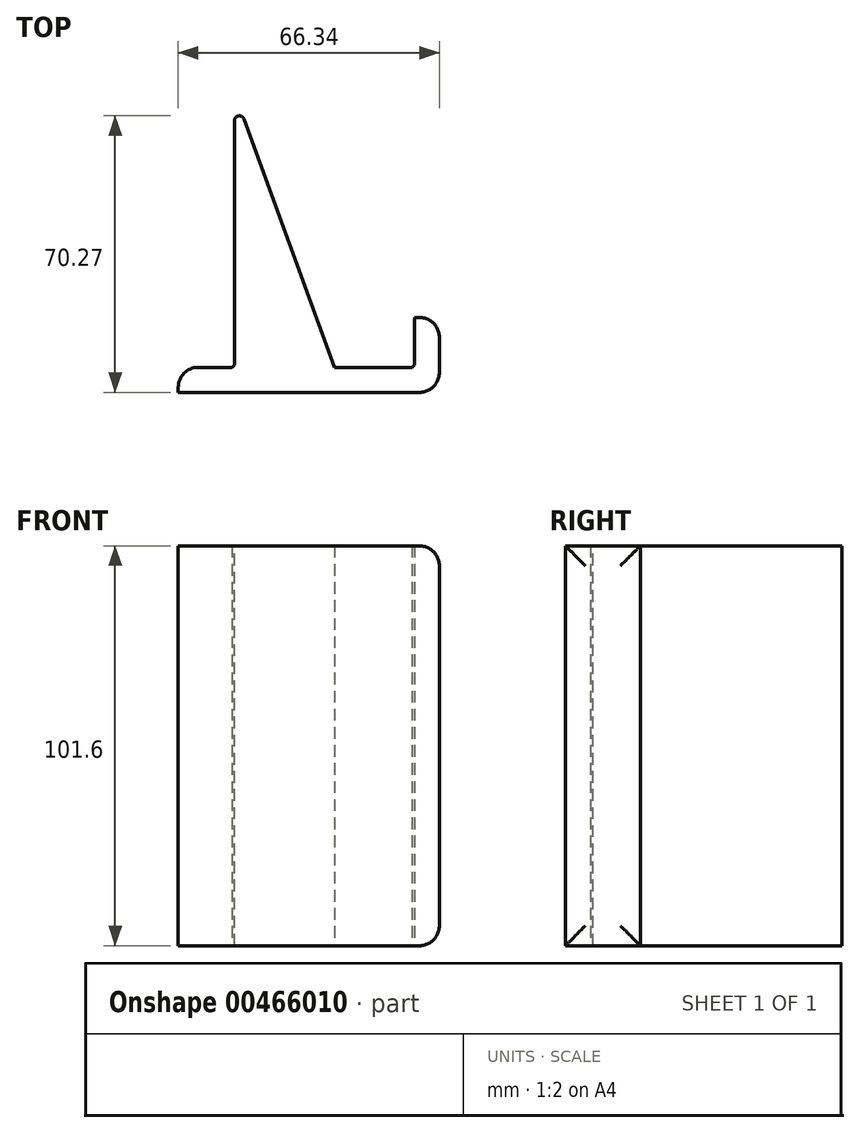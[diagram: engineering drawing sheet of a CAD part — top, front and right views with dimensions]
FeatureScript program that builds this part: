
annotation { "Feature Type Name" : "Feature", "Feature Type Description" : "" }
export const myFeature = defineFeature(function(context is Context, id is Id, definition is map)
    precondition{}
    {
        {
            var Q0;
            Q0=qCreatedBy(makeId("Top.planeOp"),FACE);
            var sketch = newSketch(context, id + "F0", { "sketchPlane" : qUnion([Q0])});
            skLineSegment(sketch, "E0", {"start": v(0, 76.2) * mm, "end": v(0, 6.35) * mm});
            skLineSegment(sketch, "E1", {"start": v(0, 6.35) * mm, "end": v(-14.25, 6.35) * mm});
            skLineSegment(sketch, "E2", {"start": v(-14.25, 6.35) * mm, "end": v(-14.25, 0) * mm});
            skLineSegment(sketch, "E3", {"start": v(-14.25, 0) * mm, "end": v(0, 0) * mm});
            skLineSegment(sketch, "E4", {"start": v(0, 0) * mm, "end": v(52.1, 0) * mm});
            skLineSegment(sketch, "E5", {"start": v(52.1, 0) * mm, "end": v(52.1, 19.05) * mm});
            skLineSegment(sketch, "E6", {"start": v(52.1, 19.05) * mm, "end": v(45.74, 19.05) * mm});
            skLineSegment(sketch, "E7", {"start": v(45.74, 19.05) * mm, "end": v(45.74, 6.35) * mm});
            skLineSegment(sketch, "E8", {"start": v(45.74, 6.35) * mm, "end": v(25.42, 6.35) * mm});
            skLineSegment(sketch, "E9", {"start": v(25.42, 6.35) * mm, "end": v(0, 76.2) * mm});
            skSolve(sketch);
        }
        {
            var Q0;
            Q0=makeQuery(id+"F0.imprint","IMPRINT",FACE,{"disambiguationData":[TD([[makeQuery(id+"F0.imprint","IMPRINT",EDGE,{"derivedFrom":sQuery(id+"F0.wireOp",EDGE,"E0")}),1.0]])]});
            extrude(context, id + "F1", {"entities" : qUnion([Q0]), "endBound" : BoundingType.SYMMETRIC, "depth" : 101.6 * mm});
        }
        {
            var Q0;
            Q0=makeQuery(id+"F1.opExtrude","SWEPT_EDGE",EDGE,{"disambiguationData":[OSD([sQuery(id+"F0.wireOp",EDGE,"E0"),sQuery(id+"F0.wireOp",EDGE,"E9")])]});
            fillet(context, id + "F2", {"entities" : qUnion([Q0]), "radius" : 1.27 * mm, "tangentPropagation" : true, "allowEdgeOverflow" : false});
        }
        {
            var Q0;
            Q0=makeQuery(id+"F1.opExtrude","SWEPT_FACE",FACE,{"disambiguationData":[OSD([sQuery(id+"F0.wireOp",EDGE,"E5")])]});
            fillet(context, id + "F3", {"entities" : qUnion([Q0]), "radius" : 5.08 * mm, "tangentPropagation" : true, "allowEdgeOverflow" : false});
        }
        {
            var Q0;
            Q0=makeQuery(id+"F1.opExtrude","SWEPT_EDGE",EDGE,{"disambiguationData":[OSD([sQuery(id+"F0.wireOp",EDGE,"E7"),sQuery(id+"F0.wireOp",EDGE,"E8")])]});
            var Q1;
            Q1=makeQuery(id+"F1.opExtrude","SWEPT_EDGE",EDGE,{"disambiguationData":[OSD([sQuery(id+"F0.wireOp",EDGE,"E0"),sQuery(id+"F0.wireOp",EDGE,"E1")])]});
            chamfer(context, id + "F4", {"entities" : qUnion([Q0, Q1]), "width" : 0.64 * mm, "tangentPropagation" : true});
        }
        {
            var Q0;
            Q0=makeQuery(id+"F1.opExtrude","SWEPT_EDGE",EDGE,{"disambiguationData":[OSD([sQuery(id+"F0.wireOp",EDGE,"E1"),sQuery(id+"F0.wireOp",EDGE,"E2")])]});
            fillet(context, id + "F5", {"entities" : qUnion([Q0]), "radius" : 5.08 * mm, "tangentPropagation" : true, "allowEdgeOverflow" : false});
        }
    });
